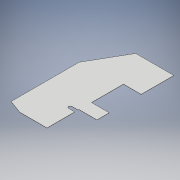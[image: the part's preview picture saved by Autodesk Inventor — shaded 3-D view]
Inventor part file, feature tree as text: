
AUTODESK INVENTOR PART (.ipt)
format: ipt  version: 2018 (Build 220112000, 112)  size: 117,760 bytes
history: native  units: mm
features: extrude x1, sketch x1
ambient origin geometry x8: Origin, YZ Plane, XZ Plane, XY Plane, X Axis, Y Axis, Z Axis, Center Point
bodies: Solid1 (feature_tree)
feature tree (2):
  extrude  "Extrusion1"  Depth=25.0mm
  sketch  "Sketch1"  dims[d0=200.0mm d1=27.925268mm d2=500.0mm d3=100.0mm d4=60.0deg d5=280.0mm d6=800.0mm d7=240.0mm d8=130.0mm d9=235.0mm d10=130.0mm d11=235.0mm d12=1.6mm d13=0.0mm d14=25.0mm d16=216.0mm d17=0.0mm d18=45.0mm]
